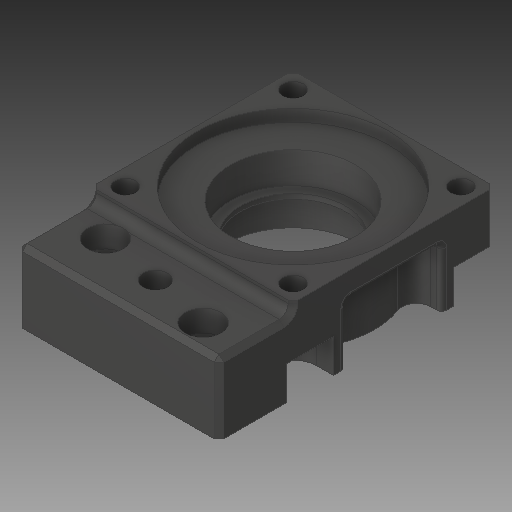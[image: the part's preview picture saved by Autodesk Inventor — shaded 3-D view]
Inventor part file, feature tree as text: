
AUTODESK INVENTOR PART (.ipt)
format: ipt  version: 2019 (Build 230136000, 136)  size: 259,584 bytes
history: native  units: in
note: dims shown in document units (in); Inventor stores cm internally (conversion verified against a paired STEP export)
features: fillet x1
ambient origin geometry x8: Origin, YZ Plane, XZ Plane, XY Plane, X Axis, Y Axis, Z Axis, Center Point
bodies: Solid1 (feature_tree)
feature tree (1):
  fillet  "Fillet5"  [1 undecoded]
note: 1 required parameter value undecoded (feature->parameter linkage not recoverable at this tier; creation-order binding heuristic only, values carry confidence <= 0.55)
